# Revit family: Comfort_Window_D_Side_Hung_Standard
name_source: partatom
category: Windows
revit_build: Autodesk Revit 2014 (Build: 20130308_1515(x64)
units: mm (PartAtom-declared; Revit-internal decimal feet)

## types (2) — shared parameters
DG Gasket Thickness = 12 mm  [stored 0.0393701 ft]
Description = Comfort Window, Side Hung, Type D
Double Glazing Gasket Finish = Double Glazing Gasket Material
Frame Depth = 33 mm
Frame Edge Thickness = 26 mm
Limit Fixed Pane Height Max = 1800 mm
Limit Fixed Pane Height Min = 200 mm
Limit Fixed Pane Width Max = 1800 mm
Limit Fixed Pane Width Min = 200 mm
Limit Sash Height Max = 1200 mm
Limit Sash Height Min = 300 mm  [stored 0.984252 ft]
Limit Sash Width Max = 600 mm  [stored 1.9685 ft]
Limit Sash Width Min = 300 mm  [stored 0.984252 ft]
Limit Window Width Max = 675 mm  [stored 2.21457 ft]
Limit Window Width Min = 375 mm
Manufacturer = Crealco
Max System DG One Piece Thickness = 4 mm  [stored 0.0131234 ft]
Max System DG Unit Thickness = 20 mm  [stored 0.0656168 ft]
Model = Comfort Window
Rough Height = 1647 mm
Rough Width = 2226 mm
Sash Frame Gap = 5 mm  [stored 0.0164042 ft]
Sash Frame Side Gap = 12 mm  [stored 0.0393701 ft]
Sash Side Gap = 38 mm
Set Sash Height = 1115 mm
Transom Height = 27 mm  [stored 0.0885827 ft]
URL = http://www.crealco.co.za
Window Width = 590 mm  [stored 1.9357 ft]
zero-valued in all types: Visual Light Transmittance

## per-type parameters (varying)
| type | Clearvue SHGC Value | Clearvue U Value | Energy Advantage SHGC Value | Energy Advantage U Value | Intruderprufe LowE SHGC Value | Intruderprufe LowE U Value | Intruderprufe SHGC Value | Intruderprufe U Value | SmartGlass Elite SHGC Value | SmartGlass Elite U Value | SmartGlass Plus SHGC Value | SmartGlass Plus U Value | SmartGlass Standard SHGC Value | SmartGlass Standard U Value | SmartGlass Superior SHGC Value | SmartGlass Superior U Value | Window Height |
| Comfort-0615S | 0.558 | 6.1 | 0.501 | 4.79 | 0.475 | 4.67 | 0.531 | 6 | 0.275 | 3.54 | 0.373 | 3.67 | 0.499 | 4.16 | 0.241 | 3.54 | 1490 mm  [stored 4.88845 ft] |
| Comfort-0618S | 0.585 | 6.08 | 0.525 | 4.69 | 0.496 | 4.57 | 0.556 | 5.98 | 0.287 | 3.37 | 0.39 | 3.51 | 0.522 | 4.03 | 0.25 | 3.38 | 1790 mm |

note: [stored X ft] marks values corroborated as IEEE doubles in the binary element streams (Revit-internal decimal feet)

## geometry (parser evidence)
native form markers: Sweep x22
no freeform markers — native parametric forms only
